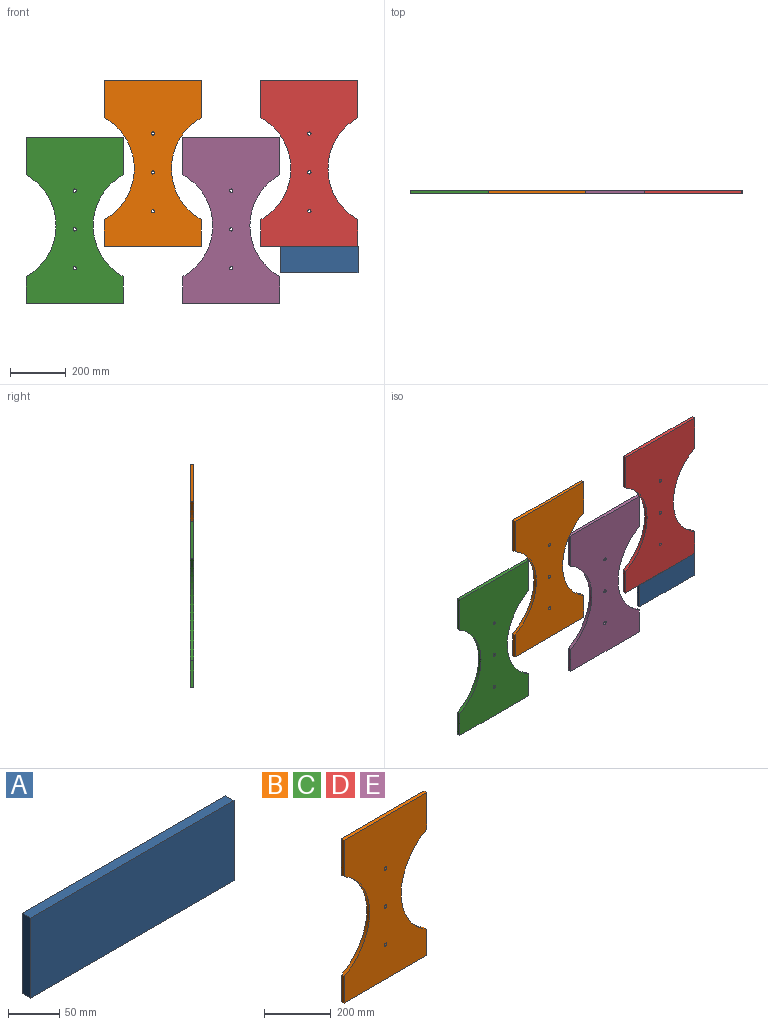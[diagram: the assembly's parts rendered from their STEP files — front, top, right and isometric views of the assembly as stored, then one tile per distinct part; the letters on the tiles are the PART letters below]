
ASSEMBLY  parts=5 mates=6
PART A: 6 faces, bbox 279.4x11.9x95.3 mm
  f0: plane 95.25x11.91mm, normal (-1,0,0), area 1134.1mm2, adj f1,f3,f4,f5
  f1: plane 279.4x11.91mm, normal (0,0,-1), area 3326.6mm2, adj f0,f2,f4,f5
  f2: plane 95.25x11.91mm, normal (1,0,0), area 1134.1mm2, adj f1,f3,f4,f5
  f3: plane 279.4x11.91mm, normal (0,0,1), area 3326.6mm2, adj f0,f2,f4,f5
  f4: plane 279.4x95.25mm, normal (0,-1,0), area 26612.8mm2, adj f0,f1,f2,f3
  f5: plane 279.4x95.25mm, normal (0,1,0), area 26612.8mm2, adj f0,f1,f2,f3
PART B: 13 faces, bbox 349.3x11.9x596.1 mm
  f0: plane 133.47x11.91mm, normal (-1,0,0), area 1589.1mm2, adj f1,f7,f8,f9
  f1: cylinder r=209.55mm len=366.54mm, axis (0,1,0), area 5312.3mm2, adj f0,f2,f8,f9
  f2: plane 96.13x11.91mm, normal (-1,0,0), area 1144.5mm2, adj f1,f3,f8,f9
  f3: plane 349.25x11.91mm, normal (0,0,-1), area 4158.3mm2, adj f2,f4,f8,f9
  f4: plane 96.13x11.91mm, normal (1,0,0), area 1144.5mm2, adj f3,f5,f8,f9
  f5: cylinder r=209.55mm len=366.54mm, axis (0,1,0), area 5312.3mm2, adj f4,f6,f8,f9
  f6: plane 133.47x11.91mm, normal (1,0,0), area 1589.1mm2, adj f5,f7,f8,f9
  f7: plane 349.25x11.91mm, normal (0,0,1), area 4158.3mm2, adj f0,f6,f8,f9
  f8: plane 596.14x349.25mm, normal (0,-1,0), area 151633.7mm2, adj f0,f1,f2,f3,f4,f5,f6,f7
  f9: plane 596.14x349.25mm, normal (0,1,0), area 151633.7mm2, adj f0,f1,f2,f3,f4,f5,f6,f7
  f10: cylinder r=5.75mm len=11.91mm, axis (0,-1,0), area 430.5mm2, adj f8,f9
  f11: cylinder r=5.75mm len=11.91mm, axis (0,-1,0), area 430.5mm2, adj f8,f9
  f12: cylinder r=5.75mm len=11.91mm, axis (0,-1,0), area 430.5mm2, adj f8,f9
PART C: same geometry as B
PART D: same geometry as B
PART E: same geometry as B
PLACE A t=(518.43,-108.42,-350.84)mm
PLACE B t=(-24.13,-108.42,74.82)mm
PLACE C t=(-305.27,-108.42,-130.06)mm
PLACE D t=(538.41,-108.42,74.82)mm
PLACE E t=(257.94,-108.42,-130.06)mm
MATE fastened A.f4 <-> D.f8  axis (0,-1,0) through (693.97,-120.33,-301.52)mm
MATE planar E.f7 <-> C.f7  axis (0,0,1) through (238.87,-114.38,89.74)mm
MATE planar E.f8 <-> B.f8  axis (0,-1,0) through (413.5,-120.33,89.74)mm
MATE planar D.f8 <-> C.f8  axis (0,-1,0) through (344.72,-120.33,294.62)mm
MATE planar C.f8 <-> B.f8  axis (0,-1,0) through (-498.96,-120.33,89.74)mm
MATE planar B.f7 <-> D.f7  axis (0,0,1) through (-43.19,-114.38,294.62)mm
